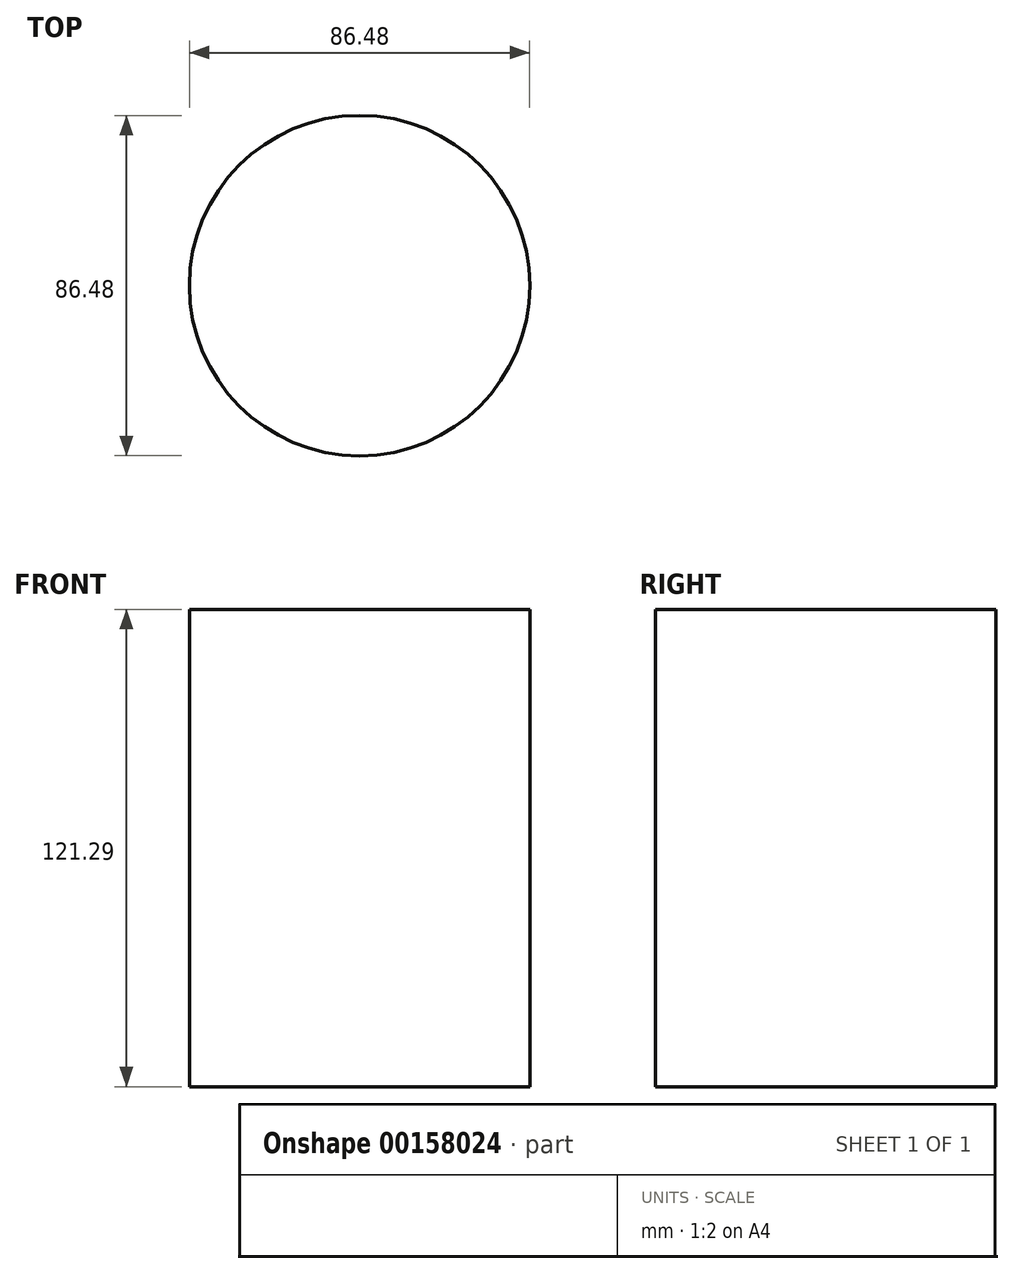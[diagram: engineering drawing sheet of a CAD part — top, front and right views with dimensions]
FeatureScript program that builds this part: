
annotation { "Feature Type Name" : "Feature", "Feature Type Description" : "" }
export const myFeature = defineFeature(function(context is Context, id is Id, definition is map)
    precondition{}
    {
        {
            var Q0;
            Q0=qCreatedBy(makeId("Top.planeOp"),FACE);
            var sketch = newSketch(context, id + "F0", { "sketchPlane" : qUnion([Q0])});
            skCircle(sketch, "E0", {"center": v(0, 0) * mm, "radius": 43.24 * mm});
            skSolve(sketch);
        }
        {
            var Q0;
            Q0 = qSketchRegion(id + "F0", true);
            extrude(context, id + "F1", {"entities" : qUnion([Q0]), "depth" : 121.28 * mm});
        }
    });
